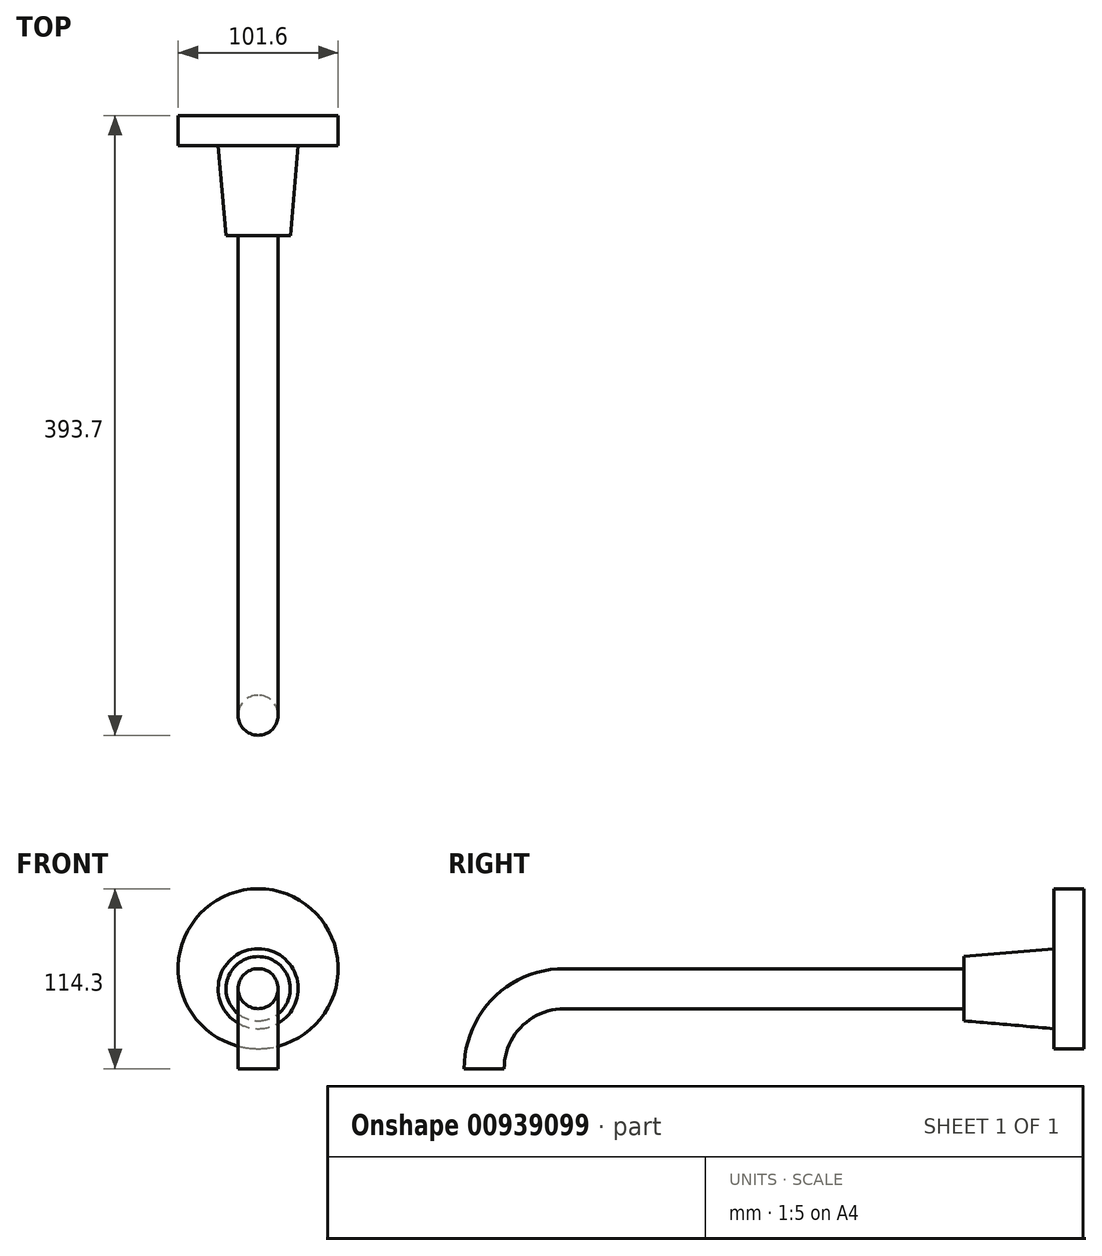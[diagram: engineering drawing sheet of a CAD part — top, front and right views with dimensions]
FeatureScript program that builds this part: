
annotation { "Feature Type Name" : "Feature", "Feature Type Description" : "" }
export const myFeature = defineFeature(function(context is Context, id is Id, definition is map)
    precondition{}
    {
        {
            var Q0;
            Q0=qCreatedBy(makeId("Front.planeOp"),FACE);
            var sketch = newSketch(context, id + "F0", { "sketchPlane" : qUnion([Q0])});
            skCircle(sketch, "E0", {"center": v(0, 0) * mm, "radius": 50.8 * mm});
            skSolve(sketch);
        }
        {
            var Q0;
            Q0=qSketchRegion(id+"F0",true);
            extrude(context, id + "F1", {"entities" : qUnion([Q0]), "depth" : 19.05 * mm, "offsetDistance" : 25.4 * mm});
        }
        {
            var Q0;
            Q0=makeQuery(id+"F1.opExtrude","CAP_FACE",FACE,{"disambiguationData":[OSD([sQuery(id+"F0.wireOp",EDGE,"E0")])],"isStart":false});
            var sketch = newSketch(context, id + "F2", { "sketchPlane" : qUnion([Q0])});
            skLineSegment(sketch, "E1", {"start": v(0, 0) * mm, "end": v(0, -50.8) * mm, "construction": true});
            skCircle(sketch, "E2", {"center": v(0, -12.7) * mm, "radius": 25.4 * mm});
            skSolve(sketch);
        }
        {
            var Q0;
            Q0=qSketchRegion(id+"F2",true);
            extrude(context, id + "F3", {"entities" : qUnion([Q0]), "operationType" : NewBodyOperationType.ADD, "depth" : 57.15 * mm, "offsetDistance" : 25.4 * mm, "hasDraft" : true, "draftAngle" : 5 * degree, "draftPullDirection" : true});
        }
        {
            var Q0;
            Q0=makeQuery(id+"F3.opExtrude","CAP_FACE",FACE,{"disambiguationData":[OSD([sQuery(id+"F2.wireOp",EDGE,"E2")])],"isStart":false});
            var sketch = newSketch(context, id + "F4", { "sketchPlane" : qUnion([Q0])});
            skCircle(sketch, "E3", {"center": v(0, -12.7) * mm, "radius": 12.7 * mm});
            skSolve(sketch);
        }
        {
            var Q0;
            Q0=qSketchRegion(id+"F4",true);
            extrude(context, id + "F5", {"entities" : qUnion([Q0]), "operationType" : NewBodyOperationType.ADD, "depth" : 254 * mm, "offsetDistance" : 25.4 * mm});
        }
        {
            var Q0;
            Q0=makeQuery(id+"F5.opExtrude","CAP_FACE",FACE,{"disambiguationData":[OSD([sQuery(id+"F4.wireOp",EDGE,"E3")])],"isStart":false});
            var sketch = newSketch(context, id + "F6", { "sketchPlane" : qUnion([Q0])});
            skCircle(sketch, "E4", {"center": v(0, -12.7) * mm, "radius": 12.7 * mm});
            skSolve(sketch);
        }
        {
            var Q0;
            Q0=qCreatedBy(makeId("Right.planeOp"),FACE);
            var sketch = newSketch(context, id + "F7", { "sketchPlane" : qUnion([Q0])});
            skArc(sketch, "E5", {"start": v(-330.2, -12.7) * mm, "mid": v(-366.12, -27.58) * mm, "end": v(-381, -63.5) * mm});
            skSolve(sketch);
        }
        {
            var Q0;
            Q0=qSketchRegion(id+"F6",true);
            var Q1;
            Q1=qConstructionFilter(qBodyType(qCreatedBy(id+"F7",EDGE),BodyType.WIRE),ConstructionObject.NO);
            sweep(context, id + "F8", {"operationType" : NewBodyOperationType.ADD, "profiles" : qUnion([Q0]), "path" : qUnion([Q1])});
        }
        {
            var Q0;
            Q0=qCreatedBy(makeId("Right.planeOp"),FACE);
            var sketch = newSketch(context, id + "F9", { "sketchPlane" : qUnion([Q0])});
            skLineSegment(sketch, "E6", {"start": v(-381, -63.5) * mm, "end": v(-381, -266.7) * mm, "construction": true});
            skLineSegment(sketch, "E7", {"start": v(-381, -63.5) * mm, "end": v(-400.05, -63.5) * mm});
            skLineSegment(sketch, "E8", {"start": v(-400.05, -63.5) * mm, "end": v(-400.05, -76.2) * mm});
            skLineSegment(sketch, "E9", {"start": v(-400.05, -76.2) * mm, "end": v(-406.4, -82.55) * mm});
            skLineSegment(sketch, "E10", {"start": v(-406.4, -82.55) * mm, "end": v(-406.4, -88.9) * mm});
            skLineSegment(sketch, "E11", {"start": v(-406.4, -88.9) * mm, "end": v(-412.75, -88.9) * mm});
            skLineSegment(sketch, "E12", {"start": v(-549.28, -260.35) * mm, "end": v(-558.8, -260.35) * mm});
            skLineSegment(sketch, "E13", {"start": v(-558.8, -260.35) * mm, "end": v(-558.8, -266.7) * mm});
            skLineSegment(sketch, "E14", {"start": v(-431.8, -158.75) * mm, "end": v(-527.25, -190.5) * mm});
            skLineSegment(sketch, "E15", {"start": v(-527.25, -190.5) * mm, "end": v(-549.27, -260.35) * mm});
            skLineSegment(sketch, "E16", {"start": v(-412.75, -88.9) * mm, "end": v(-419.1, -146.05) * mm});
            skLineSegment(sketch, "E17", {"start": v(-419.1, -146.05) * mm, "end": v(-431.8, -158.75) * mm});
            skSolve(sketch);
        }
        {
            var Q0;
            Q0=sQuery(id+"F9.wireOp",EDGE,"E7");
            var Q1;
            Q1=sQuery(id+"F9.wireOp",EDGE,"E8");
            var Q2;
            Q2=sQuery(id+"F9.wireOp",EDGE,"E9");
            var Q3;
            Q3=sQuery(id+"F9.wireOp",EDGE,"E10");
            var Q4;
            Q4=sQuery(id+"F9.wireOp",EDGE,"E11");
            var Q5;
            Q5=sQuery(id+"F9.wireOp",EDGE,"E16");
            var Q6;
            Q6=sQuery(id+"F9.wireOp",EDGE,"E17");
            var Q7;
            Q7=sQuery(id+"F9.wireOp",EDGE,"E14");
            var Q8;
            Q8=sQuery(id+"F9.wireOp",EDGE,"E15");
            var Q9;
            Q9=sQuery(id+"F9.wireOp",EDGE,"E12");
            var Q10;
            Q10=sQuery(id+"F9.wireOp",EDGE,"E13");
            var Q11;
            Q11=sQuery(id+"F9.wireOp",EDGE,"2D58C78v-TrOA-RJkM-MVeZ-I1RtM4JCcqHy");
            var Q12;
            Q12=sQuery(id+"F9.wireOp",EDGE,"E6");
            revolve(context, id + "F10", {"bodyType" : ToolBodyType.SURFACE, "surfaceOperationType" : NewSurfaceOperationType.NEW, "surfaceEntities" : qUnion([Q0, Q1, Q2, Q3, Q4, Q5, Q6, Q7, Q8, Q9, Q10, Q11]), "axis" : qUnion([Q12]), "revolveType" : RevolveType.FULL});
        }
    });
